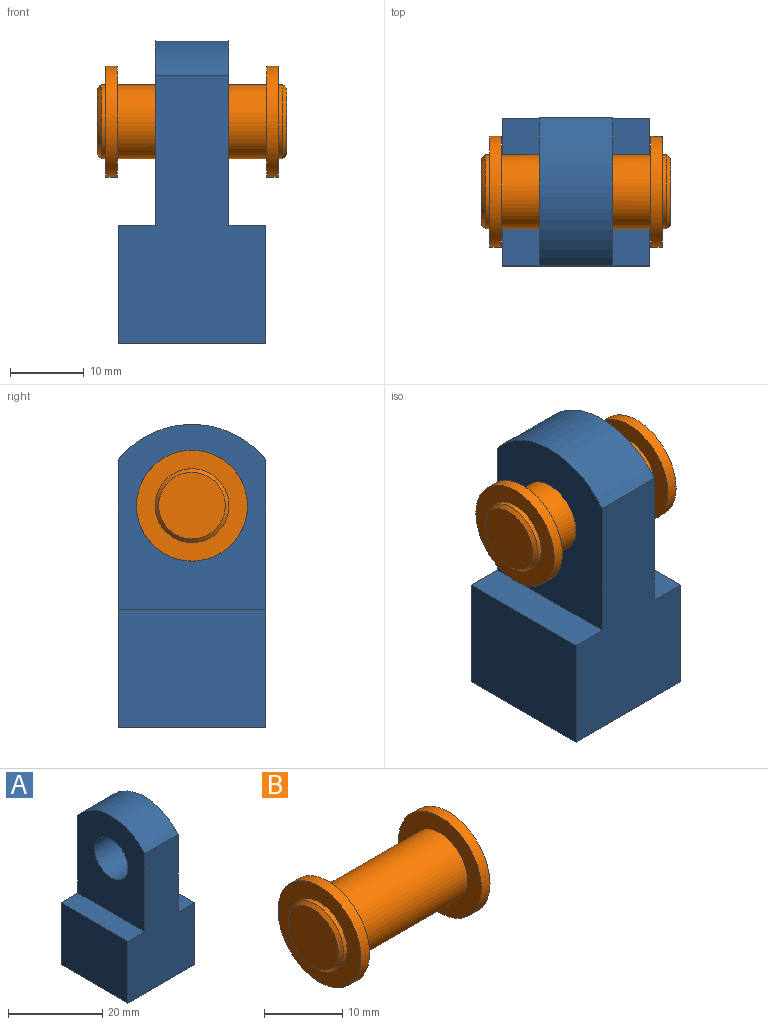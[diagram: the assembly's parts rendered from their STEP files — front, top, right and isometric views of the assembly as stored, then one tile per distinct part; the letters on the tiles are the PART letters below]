
ASSEMBLY  parts=2 mates=1
PART A: 16 faces, bbox 20x20x41 mm
  f0: plane 20x16mm, normal (-1,0,0), area 320mm2, adj f1,f3,f4,f13
  f1: plane 36.19x20mm, normal (0,-1,0), area 521.9mm2, adj f0,f2,f4,f11,f12,f13,f14,f15
  f2: plane 20x16mm, normal (1,0,0), area 320mm2, adj f1,f3,f4,f15
  f3: plane 36.19x20mm, normal (0,1,0), area 521.9mm2, adj f0,f2,f4,f11,f12,f13,f14,f15
  f4: plane 20x20mm, normal (0,0,-1), area 299.1mm2, adj f0,f1,f2,f3,f9
  f5: plane 10x10mm, normal (0,0,-1), area 12.1mm2, adj f6,f8
  f6: cylinder r=5mm len=10mm, axis (0,0,-1), area 308.9mm2, adj f5,f9
  f7: plane 9.2x9.2mm, normal (0,0,-1), area 66.5mm2, adj f8
  f8: cylinder r=4.6mm len=9.2mm, axis (0,0,-1), area 159mm2, adj f5,f7
  f9: cone r=5mm half-angle=45deg, axis (0,0,-1), area 31.6mm2, adj f4,f6
  f10: cylinder r=5mm len=10mm, axis (1,0,0), area 314.2mm2, adj f12,f14
  f11: cylinder r=12.8mm len=20mm, axis (1,0,0), area 229.5mm2, adj f1,f3,f12,f14
  f12: plane 25x20mm, normal (-1,0,0), area 392.3mm2, adj f1,f3,f10,f11,f13
  f13: plane 20x5mm, normal (0,0,1), area 100mm2, adj f0,f1,f3,f12
  f14: plane 25x20mm, normal (1,0,0), area 392.3mm2, adj f1,f3,f10,f11,f15
  f15: plane 20x5mm, normal (0,0,1), area 100mm2, adj f1,f2,f3,f14
PART B: 13 faces, bbox 25.6x15x15 mm
  f0: cylinder r=5mm len=20.2mm, axis (-1,0,0), area 634.6mm2, adj f1,f7
  f1: plane 15x15mm, normal (1,0,0), area 98.2mm2, adj f0,f3
  f2: plane 15x15mm, normal (-1,0,0), area 98.2mm2, adj f3,f6
  f3: cylinder r=7.5mm len=15mm, axis (1,0,0), area 73mm2, adj f1,f2
  f4: plane 9x9mm, normal (-1,0,0), area 63.6mm2, adj f5
  f5: cone r=5mm half-angle=45deg, axis (1,0,0), area 21.1mm2, adj f4,f6
  f6: cylinder r=5mm len=10mm, axis (-1,0,0), area 20.4mm2, adj f2,f5
  f7: plane 15x15mm, normal (-1,0,0), area 98.2mm2, adj f0,f9
  f8: plane 15x15mm, normal (1,0,0), area 98.2mm2, adj f9,f12
  f9: cylinder r=7.5mm len=15mm, axis (-1,0,0), area 73mm2, adj f7,f8
  f10: plane 9x9mm, normal (1,0,0), area 63.6mm2, adj f11
  f11: cone r=4.5mm half-angle=45deg, axis (-1,0,0), area 21.1mm2, adj f10,f12
  f12: cylinder r=5mm len=10mm, axis (-1,0,0), area 20.4mm2, adj f8,f11
PLACE A t=(-10.98,5.33,0.76)mm fixed
PLACE B t=(-10.98,5.33,30.76)mm
MATE fastened B.f0 <-> A.f10  axis (-1,0,0) through (-10.98,5.33,30.76)mm
